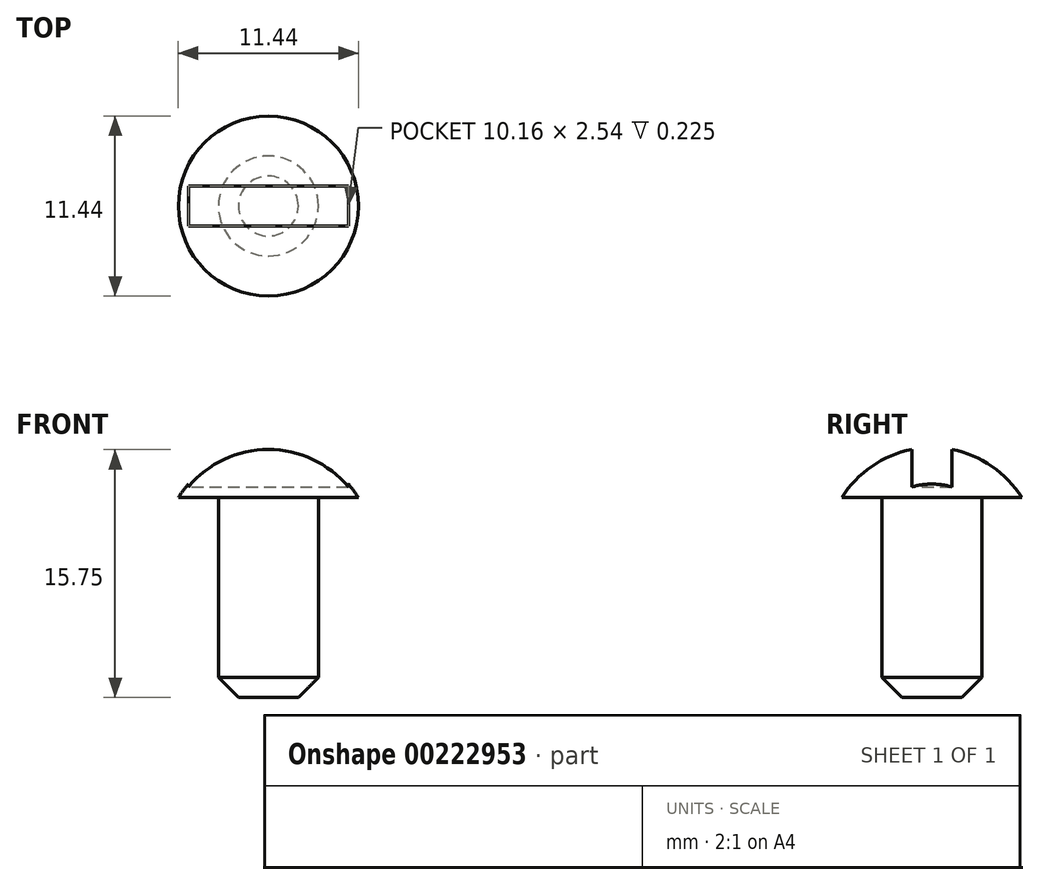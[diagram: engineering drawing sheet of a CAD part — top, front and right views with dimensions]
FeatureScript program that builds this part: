
annotation { "Feature Type Name" : "Feature", "Feature Type Description" : "" }
export const myFeature = defineFeature(function(context is Context, id is Id, definition is map)
    precondition{}
    {
        {
            var Q0;
            Q0=qCreatedBy(makeId("Front.planeOp"),FACE);
            var sketch = newSketch(context, id + "F0", { "sketchPlane" : qUnion([Q0])});
            skLineSegment(sketch, "E0", {"start": v(0, 0) * mm, "end": v(0, -11.87) * mm, "construction": true});
            skLineSegment(sketch, "E1", {"start": v(0, 15.88) * mm, "end": v(0, 0) * mm});
            skLineSegment(sketch, "E2", {"start": v(3.18, 0) * mm, "end": v(3.18, 12.7) * mm});
            skLineSegment(sketch, "E3", {"start": v(3.17, 12.7) * mm, "end": v(5.72, 12.7) * mm});
            skLineSegment(sketch, "E4", {"start": v(0, 0) * mm, "end": v(3.17, 0) * mm});
            skArc(sketch, "E5", {"start": v(0, 15.88) * mm, "mid": v(3.27, 15.03) * mm, "end": v(5.72, 12.7) * mm});
            skSolve(sketch);
        }
        {
            var Q0;
            Q0 = qSketchRegion(id + "F0", true);
            var Q1;
            Q1=sQuery(id+"F0.wireOp",EDGE,"E0");
            revolve(context, id + "F1", {"entities" : qUnion([Q0]), "axis" : qUnion([Q1]), "revolveType" : RevolveType.FULL});
        }
        {
            var Q0;
            Q0=makeQuery(id+"F1.opRevolve","SWEPT_FACE",FACE,{"disambiguationData":[OSD([sQuery(id+"F0.wireOp",EDGE,"E3")])]});
            cPlane(context, id + "F2", {"entities" : qUnion([Q0]), "cplaneType" : CPlaneType.OFFSET, "offset" : 0.64 * mm, "oppositeDirection" : true, "width" : 152.4 * mm, "height" : 152.4 * mm});
        }
        {
            var Q0;
            Q0=qCreatedBy(id+"F2.planeOp",FACE);
            var sketch = newSketch(context, id + "F3", { "sketchPlane" : qUnion([Q0])});
            skLineSegment(sketch, "E6.bottom", {"start": v(5.08, -1.27) * mm, "end": v(-5.08, -1.27) * mm});
            skLineSegment(sketch, "E6.top", {"start": v(5.08, 1.27) * mm, "end": v(-5.08, 1.27) * mm});
            skLineSegment(sketch, "E6.left", {"start": v(5.08, -1.27) * mm, "end": v(5.08, 1.27) * mm});
            skLineSegment(sketch, "E6.right", {"start": v(-5.08, -1.27) * mm, "end": v(-5.08, 1.27) * mm});
            skPoint(sketch, "E6.middle", {"position": v(0, 0) * mm});
            skSolve(sketch);
        }
        {
            var Q0;
            Q0 = qSketchRegion(id + "F3", true);
            extrude(context, id + "F4", {"entities" : qUnion([Q0]), "operationType" : NewBodyOperationType.REMOVE, "endBound" : BoundingType.THROUGH_ALL, "oppositeDirection" : true, "depth" : 25.4 * mm});
        }
        {
            var Q0;
            Q0=makeQuery(id+"F1.opRevolve","SWEPT_EDGE",EDGE,{"disambiguationData":[OSD([sQuery(id+"F0.wireOp",EDGE,"E2"),sQuery(id+"F0.wireOp",EDGE,"E4")])]});
            chamfer(context, id + "F5", {"entities" : qUnion([Q0]), "width" : 1.27 * mm, "tangentPropagation" : true});
        }
    });
